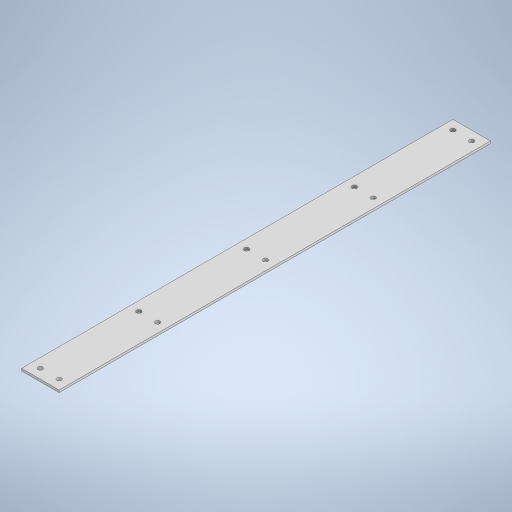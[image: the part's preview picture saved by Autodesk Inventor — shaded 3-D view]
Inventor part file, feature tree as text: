
AUTODESK INVENTOR PART (.ipt)
format: ipt  version: 2023 (Build 270158030, 158C)  size: 261,632 bytes
history: native  units: in
note: dims shown in document units (in); Inventor stores cm internally (conversion verified against a paired STEP export)
features: extrude x1, sketch x1
ambient origin geometry x8: Origin, YZ Plane, XZ Plane, XY Plane, X Axis, Y Axis, Z Axis, Center Point
bodies: Solid1 (feature_tree)
feature tree (2):
  extrude  "Extrusion1"  Depth=23.0in
  sketch  "Sketch1"  dims[d0=2.0in d1=23.0in d2=0.125in d3=0.0in d4=0.25in d5=0.5in d6=0.5in d11=0.25in d12=11.5in d13=0.25in d14=5.75in]
